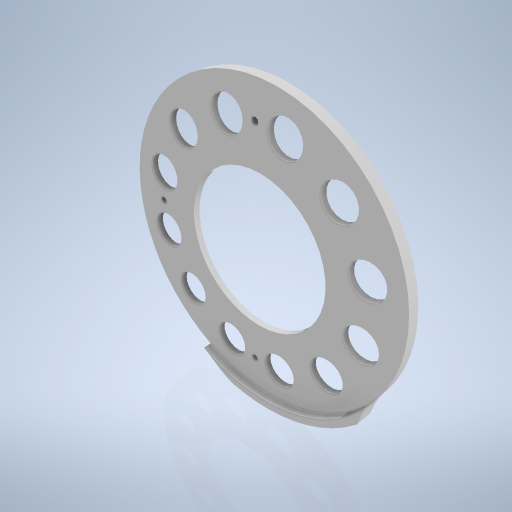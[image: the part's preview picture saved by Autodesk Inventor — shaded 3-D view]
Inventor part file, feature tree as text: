
AUTODESK INVENTOR PART (.ipt)
format: ipt  version: 2024.2 (Build 282272000, 272)  size: 333,312 bytes
history: native  units: mm
features: sketch x5, hole x3, extrude x2, pattern_circular x1
ambient origin geometry x8: Origin, YZ Plane, XZ Plane, XY Plane, X Axis, Y Axis, Z Axis, Center Point
bodies: Volumenkörper1 (feature_tree)
feature tree (11):
  extrude  "Extrusion1"  Depth=2.5mm TaperAngle=0.0deg
  hole  "Bohrung1"  [1 undecoded]
  hole  "Bohrung2"  [1 undecoded]
  pattern_circular  "Runde Anordnung1"  Count=12 Angle=360.0deg
  hole  "Bohrung3"  [1 undecoded]
  extrude  "Extrusion2"  Depth=20.0mm
  sketch  "Skizze1"  dims[d7=70.0mm d8=2.5mm d9=0.0mm]
  sketch  "Skizze3"  dims[d11=35.0mm d12=4.0mm d13=69.0mm d14=1.0mm d15=90.0deg d16=8.0mm d17=0.0mm]
  sketch  "Skizze4"  dims[d18=8.0mm d19=6.0mm d20=69.0mm d21=1.0mm d22=90.0deg d23=8.0mm d24=0.0mm d25=54.0mm]
  sketch  "Skizze5"  dims[d26=15.0deg d27=30.0deg]
  sketch  "Skizze6"  dims[d28=45.0deg d29=120.0mm d30=360.0deg d32=1.567mm d33=4.0mm d34=4.0mm d35=2.0mm d36=90.0deg d37=8.0mm d38=0.0mm d39=74.0mm d56=20.0mm d57=19.0mm d58=19.0mm d59=20.0mm d60=45.0mm d61=4.0mm d62=0.0mm]
note: 3 required parameter values undecoded (feature->parameter linkage not recoverable at this tier; creation-order binding heuristic only, values carry confidence <= 0.55)
